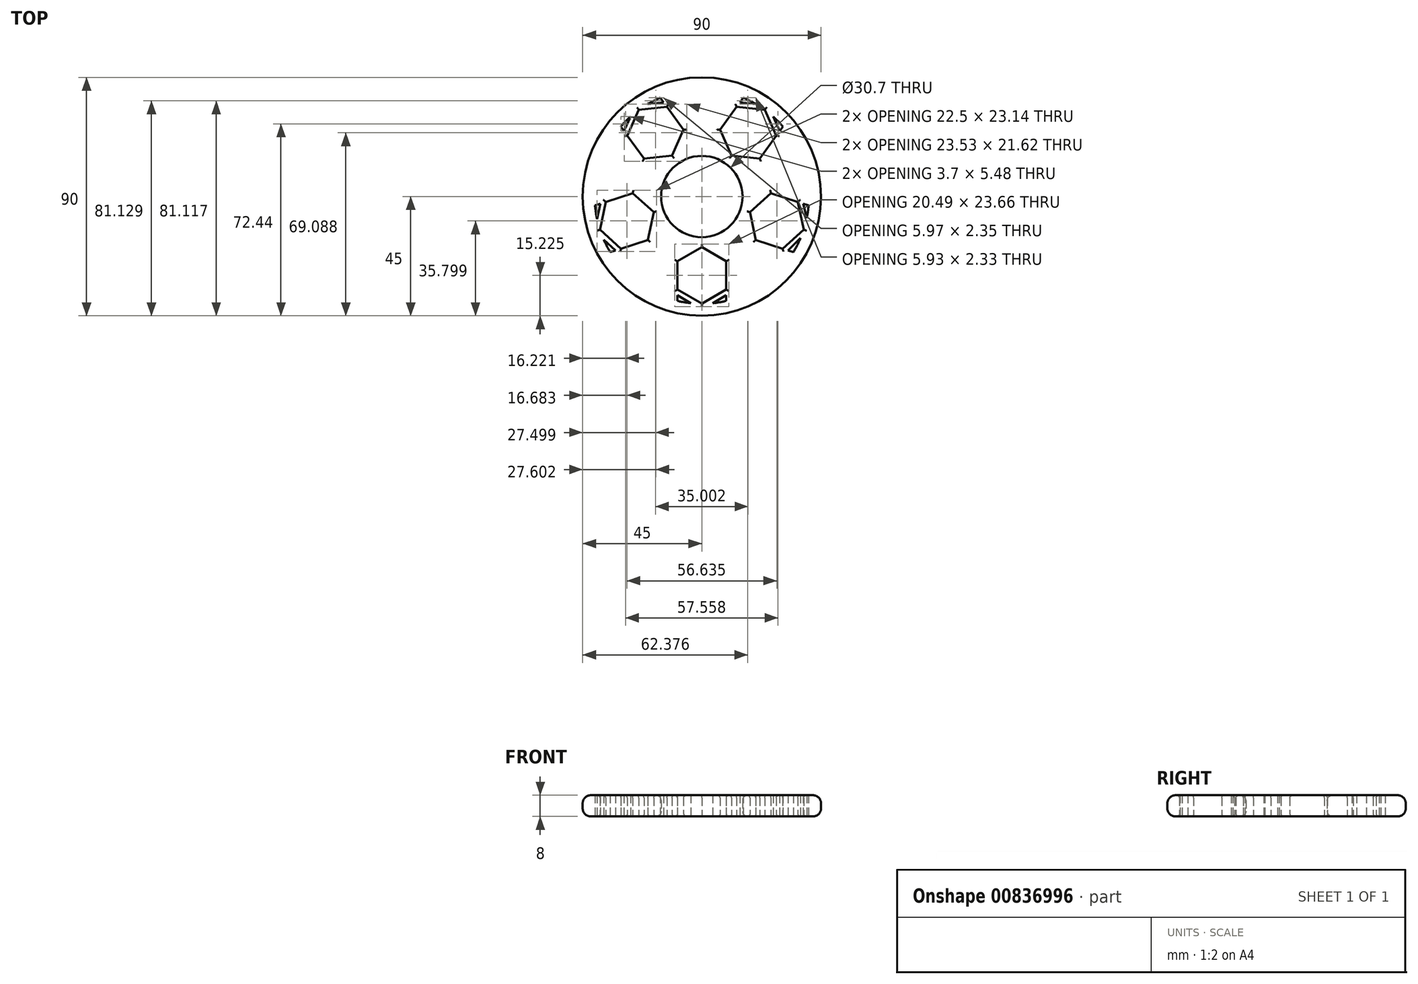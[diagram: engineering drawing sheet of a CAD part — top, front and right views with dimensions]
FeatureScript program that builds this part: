
annotation { "Feature Type Name" : "Feature", "Feature Type Description" : "" }
export const myFeature = defineFeature(function(context is Context, id is Id, definition is map)
    precondition{}
    {
        {
            var Q0;
            Q0=qCreatedBy(makeId("Top.planeOp"),FACE);
            var sketch = newSketch(context, id + "F0", { "sketchPlane" : qUnion([Q0])});
            skCircle(sketch, "E0", {"center": v(0, 0) * mm, "radius": 15.35 * mm});
            skArc(sketch, "E1.cCircle", {"start": v(-29.39, -40.45) * mm, "mid": v(47.55, -15.45) * mm, "end": v(0, 50) * mm, "construction": true});
            skPoint(sketch, "E2.orphan", {"position": v(-23.78, 32.73) * mm});
            skLineSegment(sketch, "E3.1", {"start": v(-13.16, 33.84) * mm, "end": v(-6.88, 25.2) * mm});
            skLineSegment(sketch, "E3.2", {"start": v(-6.88, 25.2) * mm, "end": v(-11.23, 15.45) * mm});
            skLineSegment(sketch, "E3.3", {"start": v(-11.23, 15.45) * mm, "end": v(-21.84, 14.33) * mm});
            skLineSegment(sketch, "E3.4", {"start": v(-21.84, 14.33) * mm, "end": v(-28.12, 22.97) * mm});
            skLineSegment(sketch, "E4.1", {"start": v(-36.25, -2.06) * mm, "end": v(-26.1, 1.24) * mm});
            skLineSegment(sketch, "E4.2", {"start": v(-26.1, 1.24) * mm, "end": v(-18.16, -5.9) * mm});
            skLineSegment(sketch, "E4.3", {"start": v(-18.16, -5.9) * mm, "end": v(-20.38, -16.34) * mm});
            skLineSegment(sketch, "E4.4", {"start": v(-20.38, -16.34) * mm, "end": v(-30.54, -19.64) * mm});
            skLineSegment(sketch, "E5.0", {"start": v(0, -19.1) * mm, "end": v(9.25, -24.44) * mm});
            skLineSegment(sketch, "E5.1", {"start": v(9.25, -24.44) * mm, "end": v(9.25, -35.11) * mm});
            skLineSegment(sketch, "E5.4", {"start": v(-9.25, -35.11) * mm, "end": v(-9.25, -24.44) * mm});
            skLineSegment(sketch, "E5.5", {"start": v(-9.25, -24.44) * mm, "end": v(0, -19.1) * mm});
            skLineSegment(sketch, "E6.0", {"start": v(18.16, -5.9) * mm, "end": v(26.1, 1.24) * mm});
            skLineSegment(sketch, "E6.1", {"start": v(26.1, 1.24) * mm, "end": v(36.25, -2.06) * mm});
            skLineSegment(sketch, "E6.4", {"start": v(30.54, -19.64) * mm, "end": v(20.38, -16.34) * mm});
            skLineSegment(sketch, "E6.5", {"start": v(20.38, -16.34) * mm, "end": v(18.16, -5.9) * mm});
            skLineSegment(sketch, "E7.0", {"start": v(11.23, 15.45) * mm, "end": v(6.88, 25.2) * mm});
            skLineSegment(sketch, "E7.1", {"start": v(6.88, 25.2) * mm, "end": v(13.16, 33.84) * mm});
            skLineSegment(sketch, "E7.4", {"start": v(28.12, 22.97) * mm, "end": v(21.84, 14.33) * mm});
            skLineSegment(sketch, "E7.5", {"start": v(21.84, 14.33) * mm, "end": v(11.23, 15.45) * mm});
            skPoint(sketch, "E8.orphan", {"position": v(-47.55, 15.45) * mm});
            skPoint(sketch, "E9.orphan", {"position": v(29.39, -40.45) * mm});
            skPoint(sketch, "E1.0.end.orphan", {"position": v(47.55, 15.45) * mm});
            skPoint(sketch, "E10.end.orphan", {"position": v(23.78, 32.73) * mm});
            skPoint(sketch, "E11.trimOffspring.end.orphan", {"position": v(-38.47, -12.5) * mm});
            skCircle(sketch, "E12", {"center": v(0, 0) * mm, "radius": 45 * mm});
            skPoint(sketch, "E13.orphan", {"position": v(0, -40.45) * mm});
            skArc(sketch, "E14", {"start": v(-15.67, 37.3) * mm, "mid": v(-18.06, 36.2) * mm, "end": v(-20.38, 34.94) * mm});
            skLineSegment(sketch, "E15", {"start": v(14.41, 35.57) * mm, "end": v(15.67, 37.3) * mm});
            skLineSegment(sketch, "E16", {"start": v(-14.41, 35.57) * mm, "end": v(-15.67, 37.3) * mm});
            skLineSegment(sketch, "E17", {"start": v(-29.37, 24.7) * mm, "end": v(-30.63, 26.42) * mm});
            skLineSegment(sketch, "E18", {"start": v(-38.28, -2.72) * mm, "end": v(-40.3, -3.38) * mm});
            skArc(sketch, "E19.trimOffspring", {"start": v(-40.3, -3.38) * mm, "mid": v(-40, -6) * mm, "end": v(-39.53, -8.59) * mm});
            skLineSegment(sketch, "E20", {"start": v(-32.57, -20.3) * mm, "end": v(-34.6, -20.96) * mm});
            skLineSegment(sketch, "E21", {"start": v(-9.25, -37.25) * mm, "end": v(-9.25, -39.38) * mm});
            skPoint(sketch, "E22.center.orphan", {"position": v(0, -29.77) * mm});
            skArc(sketch, "E23.trimOffspring", {"start": v(-9.25, -39.38) * mm, "mid": v(-6.7, -39.9) * mm, "end": v(-4.11, -40.24) * mm});
            skPoint(sketch, "E24.start.orphan", {"position": v(-18.16, -5.9) * mm});
            skPoint(sketch, "E25.center.orphan", {"position": v(-28.32, -9.2) * mm});
            skPoint(sketch, "E26.center.orphan", {"position": v(-17.5, 24.09) * mm});
            skPoint(sketch, "E27.start.orphan", {"position": v(-11.23, 15.45) * mm});
            skLineSegment(sketch, "E28", {"start": v(9.25, -37.25) * mm, "end": v(9.25, -39.38) * mm});
            skLineSegment(sketch, "E29", {"start": v(32.57, -20.3) * mm, "end": v(34.6, -20.96) * mm});
            skArc(sketch, "E30.trimOffspring", {"start": v(34.6, -20.96) * mm, "mid": v(36.03, -18.38) * mm, "end": v(37.28, -15.7) * mm});
            skLineSegment(sketch, "E31", {"start": v(38.28, -2.72) * mm, "end": v(40.3, -3.38) * mm});
            skLineSegment(sketch, "E32", {"start": v(29.37, 24.7) * mm, "end": v(30.63, 26.42) * mm});
            skArc(sketch, "E33.trimOffspring", {"start": v(30.63, 26.42) * mm, "mid": v(28.84, 28.36) * mm, "end": v(26.93, 30.18) * mm});
            skPoint(sketch, "E7.cCircle.center.orphan", {"position": v(17.5, 24.09) * mm});
            skPoint(sketch, "E34.orphan", {"position": v(38.47, -12.5) * mm});
            skPoint(sketch, "E35.center.orphan", {"position": v(28.32, -9.2) * mm});
            skLineSegment(sketch, "E36", {"start": v(-23.78, 32.73) * mm, "end": v(-28.12, 22.97) * mm});
            skLineSegment(sketch, "E37", {"start": v(-29.37, 24.7) * mm, "end": v(-26.93, 30.18) * mm});
            skArc(sketch, "E38.trimOffspring", {"start": v(-26.93, 30.18) * mm, "mid": v(-28.84, 28.36) * mm, "end": v(-30.63, 26.42) * mm});
            skLineSegment(sketch, "E39", {"start": v(-13.16, 33.84) * mm, "end": v(-23.78, 32.73) * mm});
            skLineSegment(sketch, "E40", {"start": v(-14.41, 35.57) * mm, "end": v(-20.38, 34.94) * mm});
            skLineSegment(sketch, "E41", {"start": v(13.16, 33.84) * mm, "end": v(23.78, 32.73) * mm});
            skLineSegment(sketch, "E42", {"start": v(23.78, 32.73) * mm, "end": v(28.12, 22.97) * mm});
            skLineSegment(sketch, "E43", {"start": v(38.47, -12.5) * mm, "end": v(36.25, -2.06) * mm});
            skLineSegment(sketch, "E44", {"start": v(38.47, -12.5) * mm, "end": v(30.54, -19.64) * mm});
            skLineSegment(sketch, "E45", {"start": v(-9.25, -35.11) * mm, "end": v(0, -40.45) * mm});
            skLineSegment(sketch, "E46", {"start": v(0, -40.45) * mm, "end": v(9.25, -35.11) * mm});
            skLineSegment(sketch, "E47", {"start": v(-36.25, -2.06) * mm, "end": v(-38.47, -12.5) * mm});
            skLineSegment(sketch, "E48", {"start": v(-38.47, -12.5) * mm, "end": v(-30.54, -19.64) * mm});
            skLineSegment(sketch, "E49", {"start": v(-38.28, -2.72) * mm, "end": v(-39.53, -8.59) * mm});
            skLineSegment(sketch, "E50", {"start": v(-32.57, -20.3) * mm, "end": v(-37.03, -16.29) * mm});
            skArc(sketch, "E51.trimOffspring", {"start": v(-37.03, -16.29) * mm, "mid": v(-35.89, -18.66) * mm, "end": v(-34.6, -20.96) * mm});
            skLineSegment(sketch, "E52", {"start": v(9.25, -37.25) * mm, "end": v(4.05, -40.25) * mm});
            skLineSegment(sketch, "E53", {"start": v(32.57, -20.3) * mm, "end": v(37.28, -15.7) * mm});
            skLineSegment(sketch, "E54", {"start": v(38.28, -2.72) * mm, "end": v(39.61, -8.2) * mm});
            skArc(sketch, "E55.trimOffspring", {"start": v(39.61, -8.2) * mm, "mid": v(40.03, -5.8) * mm, "end": v(40.3, -3.38) * mm});
            skArc(sketch, "E56.trimOffspring", {"start": v(4.05, -40.25) * mm, "mid": v(6.66, -39.9) * mm, "end": v(9.25, -39.38) * mm});
            skLineSegment(sketch, "E57", {"start": v(-9.25, -37.25) * mm, "end": v(-4.11, -40.24) * mm});
            skLineSegment(sketch, "E58", {"start": v(14.41, 35.57) * mm, "end": v(20.34, 34.97) * mm});
            skLineSegment(sketch, "E59", {"start": v(29.37, 24.7) * mm, "end": v(26.93, 30.18) * mm});
            skArc(sketch, "E60.trimOffspring", {"start": v(20.34, 34.97) * mm, "mid": v(18.04, 36.2) * mm, "end": v(15.67, 37.3) * mm});
            skSolve(sketch);
        }
        {
            var Q0;
            Q0 = qSketchRegion(id + "F0", true);
            extrude(context, id + "F1", {"entities" : qUnion([Q0]), "depth" : 8 * mm, "offsetDistance" : 25 * mm});
        }
        {
            var Q0;
            Q0=makeQuery(id+"F1.opExtrude","CAP_EDGE",EDGE,{"disambiguationData":[OSD([sQuery(id+"F0.wireOp",EDGE,"E7.0")])],"isStart":false});
            var Q1;
            Q1=makeQuery(id+"F1.opExtrude","CAP_EDGE",EDGE,{"disambiguationData":[OSD([sQuery(id+"F0.wireOp",EDGE,"E7.1")])],"isStart":false});
            var Q2;
            Q2=makeQuery(id+"F1.opExtrude","CAP_EDGE",EDGE,{"disambiguationData":[OSD([sQuery(id+"F0.wireOp",EDGE,"E7.5")])],"isStart":false});
            var Q3;
            Q3=makeQuery(id+"F1.opExtrude","CAP_EDGE",EDGE,{"disambiguationData":[OSD([sQuery(id+"F0.wireOp",EDGE,"E7.4")])],"isStart":false});
            var Q4;
            Q4=makeQuery(id+"F1.opExtrude","CAP_EDGE",EDGE,{"disambiguationData":[OSD([sQuery(id+"F0.wireOp",EDGE,"E42")])],"isStart":false});
            var Q5;
            Q5=makeQuery(id+"F1.opExtrude","CAP_EDGE",EDGE,{"disambiguationData":[OSD([sQuery(id+"F0.wireOp",EDGE,"E41")])],"isStart":false});
            var Q6;
            Q6=makeQuery(id+"F1.opExtrude","CAP_EDGE",EDGE,{"disambiguationData":[OSD([sQuery(id+"F0.wireOp",EDGE,"E39")])],"isStart":false});
            var Q7;
            Q7=makeQuery(id+"F1.opExtrude","CAP_EDGE",EDGE,{"disambiguationData":[OSD([sQuery(id+"F0.wireOp",EDGE,"E36")])],"isStart":false});
            var Q8;
            Q8=makeQuery(id+"F1.opExtrude","CAP_EDGE",EDGE,{"disambiguationData":[OSD([sQuery(id+"F0.wireOp",EDGE,"E3.4")])],"isStart":false});
            var Q9;
            Q9=makeQuery(id+"F1.opExtrude","CAP_EDGE",EDGE,{"disambiguationData":[OSD([sQuery(id+"F0.wireOp",EDGE,"E3.3")])],"isStart":false});
            var Q10;
            Q10=makeQuery(id+"F1.opExtrude","CAP_EDGE",EDGE,{"disambiguationData":[OSD([sQuery(id+"F0.wireOp",EDGE,"E3.2")])],"isStart":false});
            var Q11;
            Q11=makeQuery(id+"F1.opExtrude","CAP_EDGE",EDGE,{"disambiguationData":[OSD([sQuery(id+"F0.wireOp",EDGE,"E3.1")])],"isStart":false});
            var Q12;
            Q12=makeQuery(id+"F1.opExtrude","CAP_EDGE",EDGE,{"disambiguationData":[OSD([sQuery(id+"F0.wireOp",EDGE,"E6.1")])],"isStart":false});
            var Q13;
            Q13=makeQuery(id+"F1.opExtrude","CAP_EDGE",EDGE,{"disambiguationData":[OSD([sQuery(id+"F0.wireOp",EDGE,"E6.0")])],"isStart":false});
            var Q14;
            Q14=makeQuery(id+"F1.opExtrude","CAP_EDGE",EDGE,{"disambiguationData":[OSD([sQuery(id+"F0.wireOp",EDGE,"E44")])],"isStart":false});
            var Q15;
            Q15=makeQuery(id+"F1.opExtrude","CAP_EDGE",EDGE,{"disambiguationData":[OSD([sQuery(id+"F0.wireOp",EDGE,"E43")])],"isStart":false});
            var Q16;
            Q16=makeQuery(id+"F1.opExtrude","CAP_EDGE",EDGE,{"disambiguationData":[OSD([sQuery(id+"F0.wireOp",EDGE,"E6.5")])],"isStart":false});
            var Q17;
            Q17=makeQuery(id+"F1.opExtrude","CAP_EDGE",EDGE,{"disambiguationData":[OSD([sQuery(id+"F0.wireOp",EDGE,"E6.4")])],"isStart":false});
            var Q18;
            Q18=makeQuery(id+"F1.opExtrude","CAP_EDGE",EDGE,{"disambiguationData":[OSD([sQuery(id+"F0.wireOp",EDGE,"E5.0")])],"isStart":false});
            var Q19;
            Q19=makeQuery(id+"F1.opExtrude","CAP_EDGE",EDGE,{"disambiguationData":[OSD([sQuery(id+"F0.wireOp",EDGE,"E5.5")])],"isStart":false});
            var Q20;
            Q20=makeQuery(id+"F1.opExtrude","CAP_EDGE",EDGE,{"disambiguationData":[OSD([sQuery(id+"F0.wireOp",EDGE,"E5.4")])],"isStart":false});
            var Q21;
            Q21=makeQuery(id+"F1.opExtrude","CAP_EDGE",EDGE,{"disambiguationData":[OSD([sQuery(id+"F0.wireOp",EDGE,"E5.1")])],"isStart":false});
            var Q22;
            Q22=makeQuery(id+"F1.opExtrude","CAP_EDGE",EDGE,{"disambiguationData":[OSD([sQuery(id+"F0.wireOp",EDGE,"E46")])],"isStart":false});
            var Q23;
            Q23=makeQuery(id+"F1.opExtrude","CAP_EDGE",EDGE,{"disambiguationData":[OSD([sQuery(id+"F0.wireOp",EDGE,"E45")])],"isStart":false});
            var Q24;
            Q24=makeQuery(id+"F1.opExtrude","CAP_EDGE",EDGE,{"disambiguationData":[OSD([sQuery(id+"F0.wireOp",EDGE,"E4.4")])],"isStart":false});
            var Q25;
            Q25=makeQuery(id+"F1.opExtrude","CAP_EDGE",EDGE,{"disambiguationData":[OSD([sQuery(id+"F0.wireOp",EDGE,"E4.3")])],"isStart":false});
            var Q26;
            Q26=makeQuery(id+"F1.opExtrude","CAP_EDGE",EDGE,{"disambiguationData":[OSD([sQuery(id+"F0.wireOp",EDGE,"E4.2")])],"isStart":false});
            var Q27;
            Q27=makeQuery(id+"F1.opExtrude","CAP_EDGE",EDGE,{"disambiguationData":[OSD([sQuery(id+"F0.wireOp",EDGE,"E47")])],"isStart":false});
            var Q28;
            Q28=makeQuery(id+"F1.opExtrude","CAP_EDGE",EDGE,{"disambiguationData":[OSD([sQuery(id+"F0.wireOp",EDGE,"E48")])],"isStart":false});
            var Q29;
            Q29=makeQuery(id+"F1.opExtrude","CAP_EDGE",EDGE,{"disambiguationData":[OSD([sQuery(id+"F0.wireOp",EDGE,"E4.1")])],"isStart":false});
            var Q30;
            Q30=makeQuery(id+"F1.opExtrude","CAP_EDGE",EDGE,{"disambiguationData":[OSD([sQuery(id+"F0.wireOp",EDGE,"E7.1")])],"isStart":true});
            var Q31;
            Q31=makeQuery(id+"F1.opExtrude","CAP_EDGE",EDGE,{"disambiguationData":[OSD([sQuery(id+"F0.wireOp",EDGE,"E41")])],"isStart":true});
            var Q32;
            Q32=makeQuery(id+"F1.opExtrude","CAP_EDGE",EDGE,{"disambiguationData":[OSD([sQuery(id+"F0.wireOp",EDGE,"E42")])],"isStart":true});
            var Q33;
            Q33=makeQuery(id+"F1.opExtrude","CAP_EDGE",EDGE,{"disambiguationData":[OSD([sQuery(id+"F0.wireOp",EDGE,"E7.4")])],"isStart":true});
            var Q34;
            Q34=makeQuery(id+"F1.opExtrude","CAP_EDGE",EDGE,{"disambiguationData":[OSD([sQuery(id+"F0.wireOp",EDGE,"E7.5")])],"isStart":true});
            var Q35;
            Q35=makeQuery(id+"F1.opExtrude","CAP_EDGE",EDGE,{"disambiguationData":[OSD([sQuery(id+"F0.wireOp",EDGE,"E7.0")])],"isStart":true});
            var Q36;
            Q36=makeQuery(id+"F1.opExtrude","CAP_EDGE",EDGE,{"disambiguationData":[OSD([sQuery(id+"F0.wireOp",EDGE,"E3.2")])],"isStart":true});
            var Q37;
            Q37=makeQuery(id+"F1.opExtrude","CAP_EDGE",EDGE,{"disambiguationData":[OSD([sQuery(id+"F0.wireOp",EDGE,"E3.3")])],"isStart":true});
            var Q38;
            Q38=makeQuery(id+"F1.opExtrude","CAP_EDGE",EDGE,{"disambiguationData":[OSD([sQuery(id+"F0.wireOp",EDGE,"E3.4")])],"isStart":true});
            var Q39;
            Q39=makeQuery(id+"F1.opExtrude","CAP_EDGE",EDGE,{"disambiguationData":[OSD([sQuery(id+"F0.wireOp",EDGE,"E39")])],"isStart":true});
            var Q40;
            Q40=makeQuery(id+"F1.opExtrude","CAP_EDGE",EDGE,{"disambiguationData":[OSD([sQuery(id+"F0.wireOp",EDGE,"E36")])],"isStart":true});
            var Q41;
            Q41=makeQuery(id+"F1.opExtrude","CAP_EDGE",EDGE,{"disambiguationData":[OSD([sQuery(id+"F0.wireOp",EDGE,"E3.1")])],"isStart":true});
            var Q42;
            Q42=makeQuery(id+"F1.opExtrude","CAP_EDGE",EDGE,{"disambiguationData":[OSD([sQuery(id+"F0.wireOp",EDGE,"E4.2")])],"isStart":true});
            var Q43;
            Q43=makeQuery(id+"F1.opExtrude","CAP_EDGE",EDGE,{"disambiguationData":[OSD([sQuery(id+"F0.wireOp",EDGE,"E4.1")])],"isStart":true});
            var Q44;
            Q44=makeQuery(id+"F1.opExtrude","CAP_EDGE",EDGE,{"disambiguationData":[OSD([sQuery(id+"F0.wireOp",EDGE,"E47")])],"isStart":true});
            var Q45;
            Q45=makeQuery(id+"F1.opExtrude","CAP_EDGE",EDGE,{"disambiguationData":[OSD([sQuery(id+"F0.wireOp",EDGE,"E4.4")])],"isStart":true});
            var Q46;
            Q46=makeQuery(id+"F1.opExtrude","CAP_EDGE",EDGE,{"disambiguationData":[OSD([sQuery(id+"F0.wireOp",EDGE,"E4.3")])],"isStart":true});
            var Q47;
            Q47=makeQuery(id+"F1.opExtrude","CAP_EDGE",EDGE,{"disambiguationData":[OSD([sQuery(id+"F0.wireOp",EDGE,"E48")])],"isStart":true});
            var Q48;
            Q48=makeQuery(id+"F1.opExtrude","CAP_EDGE",EDGE,{"disambiguationData":[OSD([sQuery(id+"F0.wireOp",EDGE,"E5.0")])],"isStart":true});
            var Q49;
            Q49=makeQuery(id+"F1.opExtrude","CAP_EDGE",EDGE,{"disambiguationData":[OSD([sQuery(id+"F0.wireOp",EDGE,"E5.5")])],"isStart":true});
            var Q50;
            Q50=makeQuery(id+"F1.opExtrude","CAP_EDGE",EDGE,{"disambiguationData":[OSD([sQuery(id+"F0.wireOp",EDGE,"E5.4")])],"isStart":true});
            var Q51;
            Q51=makeQuery(id+"F1.opExtrude","CAP_EDGE",EDGE,{"disambiguationData":[OSD([sQuery(id+"F0.wireOp",EDGE,"E45")])],"isStart":true});
            var Q52;
            Q52=makeQuery(id+"F1.opExtrude","CAP_EDGE",EDGE,{"disambiguationData":[OSD([sQuery(id+"F0.wireOp",EDGE,"E46")])],"isStart":true});
            var Q53;
            Q53=makeQuery(id+"F1.opExtrude","CAP_EDGE",EDGE,{"disambiguationData":[OSD([sQuery(id+"F0.wireOp",EDGE,"E5.1")])],"isStart":true});
            var Q54;
            Q54=makeQuery(id+"F1.opExtrude","CAP_EDGE",EDGE,{"disambiguationData":[OSD([sQuery(id+"F0.wireOp",EDGE,"E6.4")])],"isStart":true});
            var Q55;
            Q55=makeQuery(id+"F1.opExtrude","CAP_EDGE",EDGE,{"disambiguationData":[OSD([sQuery(id+"F0.wireOp",EDGE,"E44")])],"isStart":true});
            var Q56;
            Q56=makeQuery(id+"F1.opExtrude","CAP_EDGE",EDGE,{"disambiguationData":[OSD([sQuery(id+"F0.wireOp",EDGE,"E43")])],"isStart":true});
            var Q57;
            Q57=makeQuery(id+"F1.opExtrude","CAP_EDGE",EDGE,{"disambiguationData":[OSD([sQuery(id+"F0.wireOp",EDGE,"E6.5")])],"isStart":true});
            var Q58;
            Q58=makeQuery(id+"F1.opExtrude","CAP_EDGE",EDGE,{"disambiguationData":[OSD([sQuery(id+"F0.wireOp",EDGE,"E6.0")])],"isStart":true});
            var Q59;
            Q59=makeQuery(id+"F1.opExtrude","CAP_EDGE",EDGE,{"disambiguationData":[OSD([sQuery(id+"F0.wireOp",EDGE,"E6.1")])],"isStart":true});
            fillet(context, id + "F2", {"entities" : qUnion([Q0, Q1, Q2, Q3, Q4, Q5, Q6, Q7, Q8, Q9, Q10, Q11, Q12, Q13, Q14, Q15, Q16, Q17, Q18, Q19, Q20, Q21, Q22, Q23, Q24, Q25, Q26, Q27, Q28, Q29, Q30, Q31, Q32, Q33, Q34, Q35, Q36, Q37, Q38, Q39, Q40, Q41, Q42, Q43, Q44, Q45, Q46, Q47, Q48, Q49, Q50, Q51, Q52, Q53, Q54, Q55, Q56, Q57, Q58, Q59]), "radius" : 1 * mm, "tangentPropagation" : true, "allowEdgeOverflow" : false});
        }
        {
            var Q0;
            Q0=makeQuery(id+"F1.opExtrude","CAP_EDGE",EDGE,{"disambiguationData":[OSD([sQuery(id+"F0.wireOp",EDGE,"E12")])],"isStart":false});
            var Q1;
            Q1=makeQuery(id+"F1.opExtrude","CAP_EDGE",EDGE,{"disambiguationData":[OSD([sQuery(id+"F0.wireOp",EDGE,"E12")])],"isStart":true});
            fillet(context, id + "F3", {"entities" : qUnion([Q0, Q1]), "radius" : 3 * mm, "tangentPropagation" : true, "allowEdgeOverflow" : false});
        }
        {
            var Q0;
            Q0=makeQuery(id+"F1.opExtrude","CAP_EDGE",EDGE,{"disambiguationData":[OSD([sQuery(id+"F0.wireOp",EDGE,"E0")])],"isStart":true});
            var Q1;
            Q1=makeQuery(id+"F1.opExtrude","CAP_EDGE",EDGE,{"disambiguationData":[OSD([sQuery(id+"F0.wireOp",EDGE,"E0")])],"isStart":false});
            fillet(context, id + "F4", {"entities" : qUnion([Q0, Q1]), "radius" : 2 * mm, "tangentPropagation" : true, "allowEdgeOverflow" : false});
        }
    });
